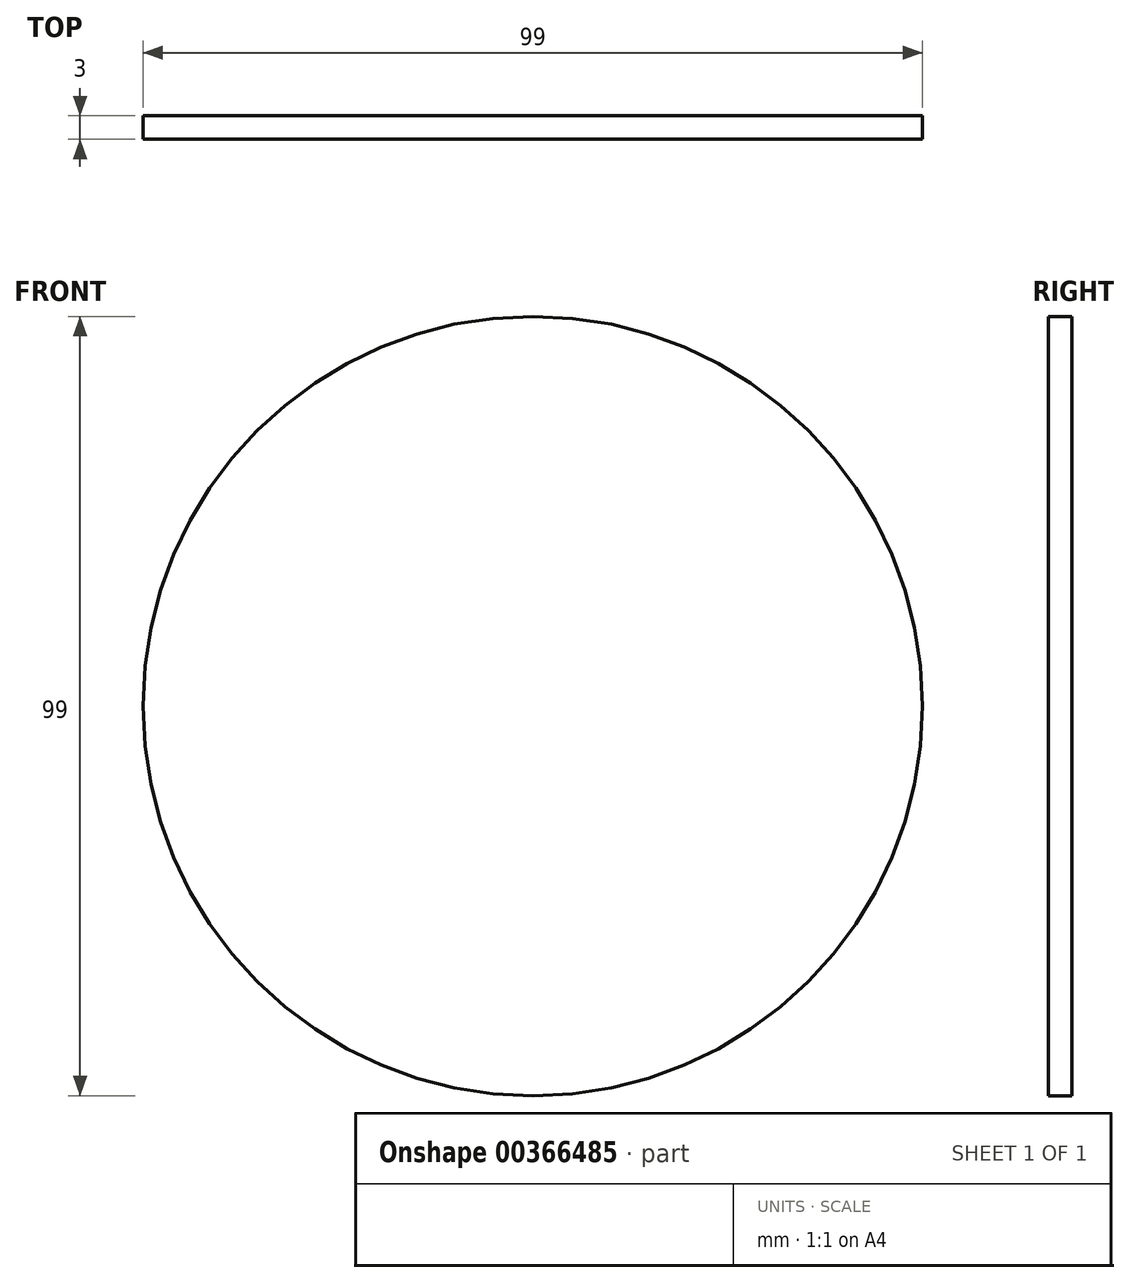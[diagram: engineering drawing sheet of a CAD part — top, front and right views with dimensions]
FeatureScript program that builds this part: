
annotation { "Feature Type Name" : "Feature", "Feature Type Description" : "" }
export const myFeature = defineFeature(function(context is Context, id is Id, definition is map)
    precondition{}
    {
        {
            var Q0;
            Q0=qCreatedBy(makeId("Front.planeOp"),FACE);
            var sketch = newSketch(context, id + "F0", { "sketchPlane" : qUnion([Q0])});
            skCircle(sketch, "E0", {"center": v(0, 0) * mm, "radius": 49.5 * mm});
            skSolve(sketch);
        }
        {
            var Q0;
            Q0=makeQuery(id+"F0.imprint","IMPRINT",FACE,{"disambiguationData":[TD([[makeQuery(id+"F0.imprint","IMPRINT",EDGE,{"derivedFrom":sQuery(id+"F0.wireOp",EDGE,"E0")}),1.0]])]});
            extrude(context, id + "F1", {"entities" : qUnion([Q0]), "depth" : 3 * mm});
        }
    });
